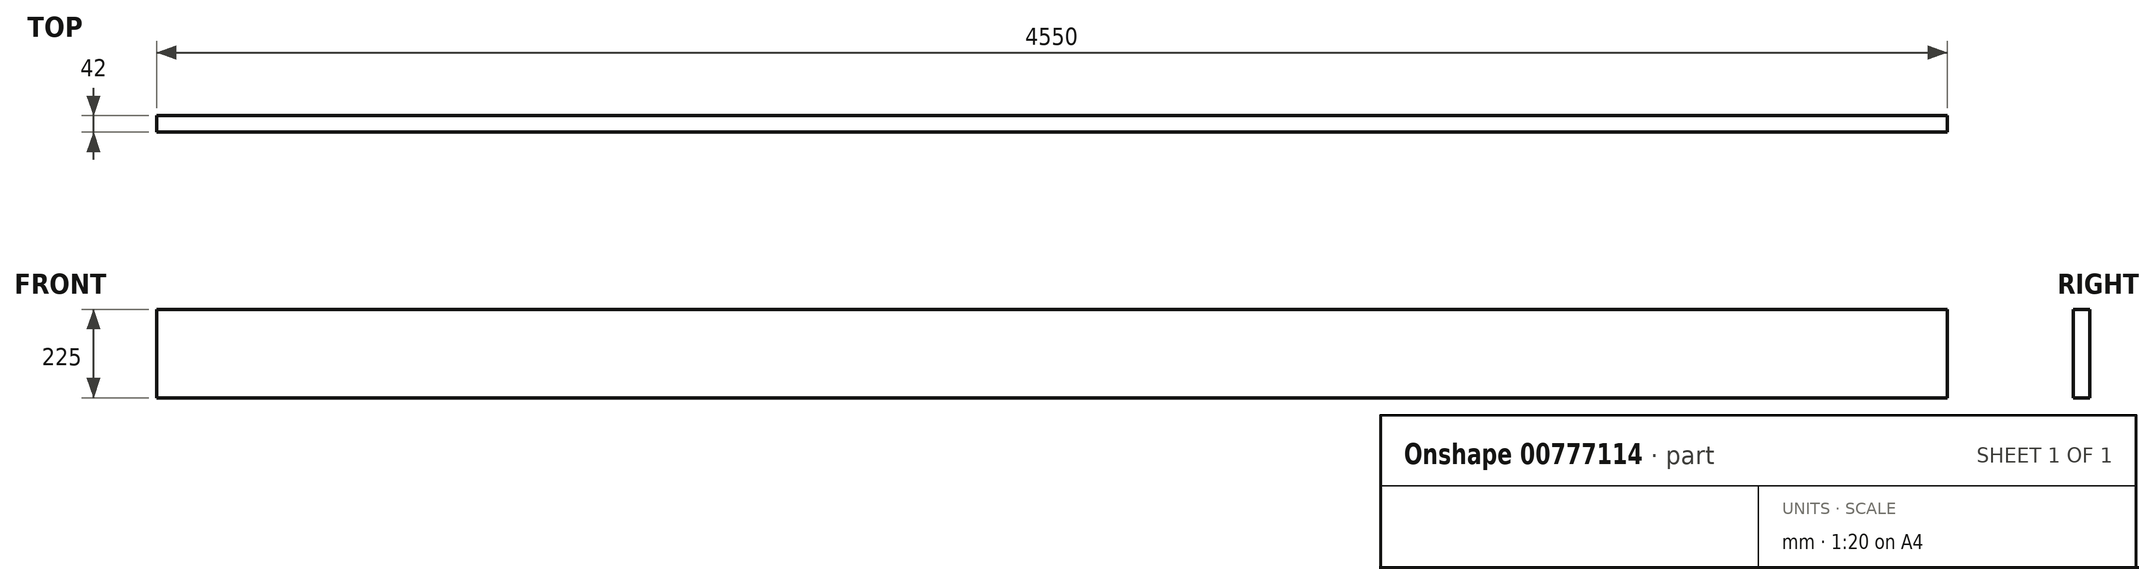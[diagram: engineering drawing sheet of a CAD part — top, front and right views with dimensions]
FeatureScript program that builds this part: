
annotation { "Feature Type Name" : "Feature", "Feature Type Description" : "" }
export const myFeature = defineFeature(function(context is Context, id is Id, definition is map)
    precondition{}
    {
        {
            var Q0;
            Q0=qCreatedBy(makeId("Right.planeOp"),FACE);
            var sketch = newSketch(context, id + "F0", { "sketchPlane" : qUnion([Q0])});
            skLineSegment(sketch, "E0.bottom", {"start": v(21, 112.5) * mm, "end": v(-21, 112.5) * mm});
            skLineSegment(sketch, "E0.top", {"start": v(21, -112.5) * mm, "end": v(-21, -112.5) * mm});
            skLineSegment(sketch, "E0.left", {"start": v(21, 112.5) * mm, "end": v(21, -112.5) * mm});
            skLineSegment(sketch, "E0.right", {"start": v(-21, 112.5) * mm, "end": v(-21, -112.5) * mm});
            skPoint(sketch, "E0.middle", {"position": v(0, 0) * mm});
            skSolve(sketch);
        }
        {
            var Q0;
            Q0=makeQuery(id+"F0.imprint","IMPRINT",FACE,{"disambiguationData":[TD([[makeQuery(id+"F0.imprint","IMPRINT",EDGE,{"derivedFrom":sQuery(id+"F0.wireOp",EDGE,"E0.bottom")}),1.0]])]});
            extrude(context, id + "F1", {"entities" : qUnion([Q0]), "oppositeDirection" : true, "depth" : 4550 * mm, "offsetDistance" : 25 * mm});
        }
    });
